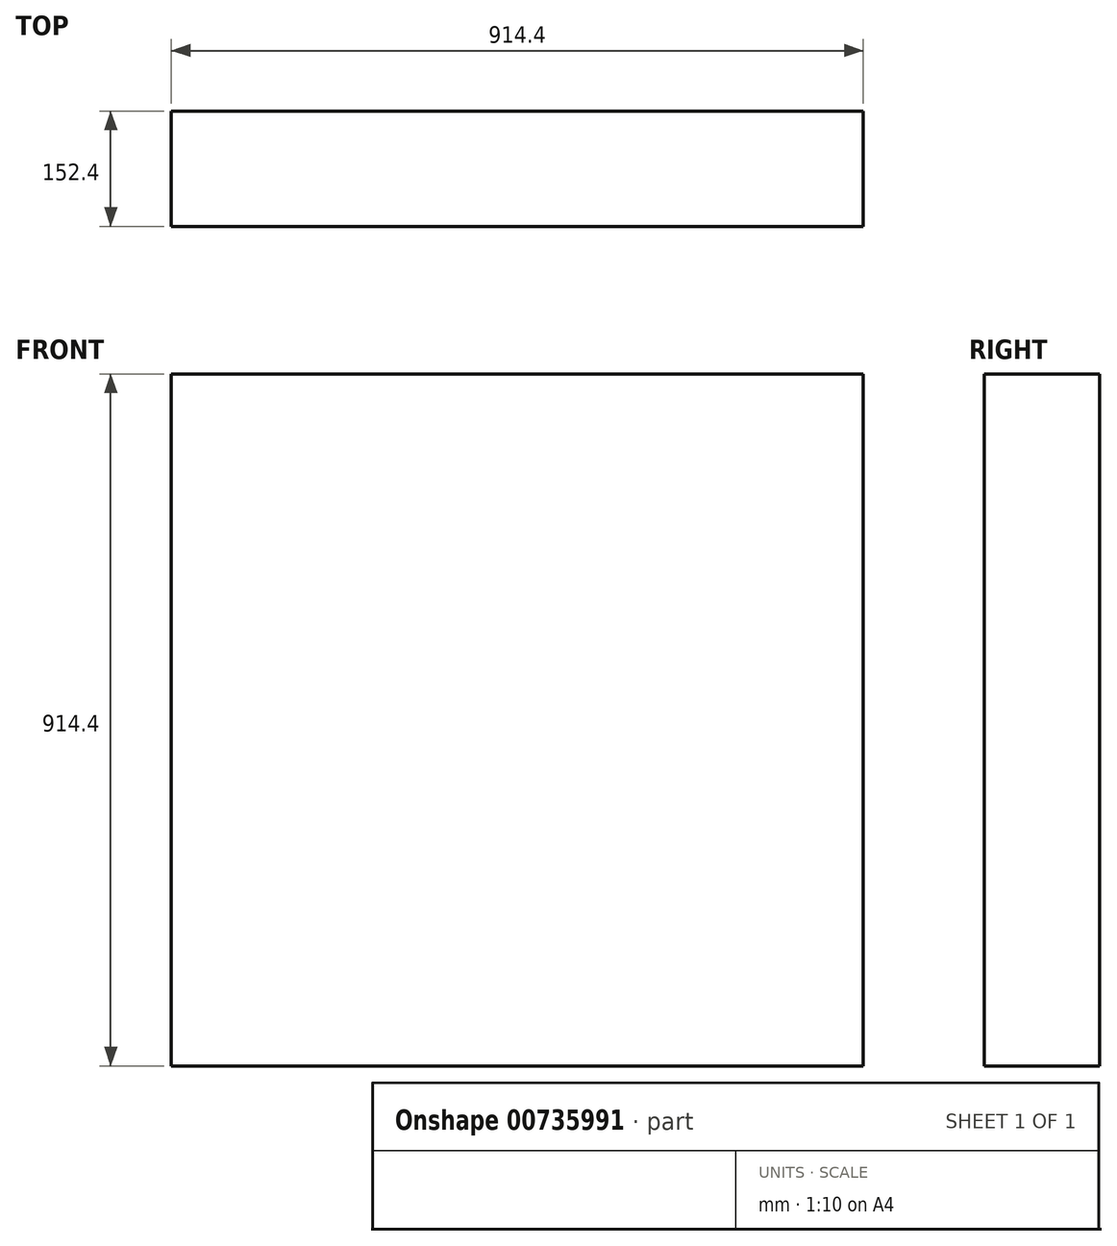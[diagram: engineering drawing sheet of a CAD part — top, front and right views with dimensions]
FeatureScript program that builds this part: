
annotation { "Feature Type Name" : "Feature", "Feature Type Description" : "" }
export const myFeature = defineFeature(function(context is Context, id is Id, definition is map)
    precondition{}
    {
        {
            assignVariable(context, id + "F0", {"name" : "transformX", "anyValue" : 0});
        }
        {
            assignVariable(context, id + "F1", {"name" : "transformY", "anyValue" : 0});
        }
        {
            assignVariable(context, id + "F2", {"name" : "transformZ", "anyValue" : 0});
        }
        {
            assignVariable(context, id + "F3", {"name" : "rotateZ", "anyValue" : 0});
        }
        {
            var Q0;
            Q0=qCreatedBy(makeId("Front.planeOp"),FACE);
            var sketch = newSketch(context, id + "F4", { "sketchPlane" : qUnion([Q0])});
            skLineSegment(sketch, "E0.bottom", {"start": v(457.2, 457.2) * mm, "end": v(-457.2, 457.2) * mm});
            skLineSegment(sketch, "E0.top", {"start": v(457.2, -457.2) * mm, "end": v(-457.2, -457.2) * mm});
            skLineSegment(sketch, "E0.left", {"start": v(457.2, 457.2) * mm, "end": v(457.2, -457.2) * mm});
            skLineSegment(sketch, "E0.right", {"start": v(-457.2, 457.2) * mm, "end": v(-457.2, -457.2) * mm});
            skPoint(sketch, "E0.middle", {"position": v(0, 0) * mm});
            skSolve(sketch);
        }
        {
            var Q0;
            Q0 = qSketchRegion(id + "F4", true);
            extrude(context, id + "F5", {"entities" : qUnion([Q0]), "endBound" : BoundingType.SYMMETRIC, "depth" : 152.4 * mm, "offsetDistance" : 25.4 * mm});
        }
        {
            var Q0;
            Q0=makeQuery(id+"F5.opExtrude","SWEPT_BODY",BODY,{"disambiguationData":[OSD([sQuery(id+"F4.wireOp",EDGE,"E0.bottom"),sQuery(id+"F4.wireOp",EDGE,"E0.top"),sQuery(id+"F4.wireOp",EDGE,"E0.left"),sQuery(id+"F4.wireOp",EDGE,"E0.right")])]});
            transform(context, id + "F6", {"entities" : qUnion([Q0]), "transformType" : TransformType.TRANSLATION_3D, "dx" : (getVariable(context, 'transformX')) * mm, "dy" : (getVariable(context, 'transformY')) * mm, "dz" : (getVariable(context, 'transformZ')) * mm, "makeCopy" : false});
        }
        {
            var Q0;
            Q0=makeQuery(id+"F5.opExtrude","SWEPT_BODY",BODY,{"disambiguationData":[OSD([sQuery(id+"F4.wireOp",EDGE,"E0.bottom"),sQuery(id+"F4.wireOp",EDGE,"E0.top"),sQuery(id+"F4.wireOp",EDGE,"E0.left"),sQuery(id+"F4.wireOp",EDGE,"E0.right")])]});
            var Q1;
            Q1=makeQuery(id+"F5.opExtrude","CAP_EDGE",EDGE,{"disambiguationData":[OSD([sQuery(id+"F4.wireOp",EDGE,"E0.left")])],"isStart":false});
            transform(context, id + "F7", {"entities" : qUnion([Q0]), "transformType" : TransformType.ROTATION, "transformAxis" : qUnion([Q1]), "angle" : (getVariable(context, 'rotateZ')) * degree, "makeCopy" : false});
        }
    });
